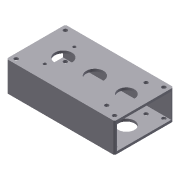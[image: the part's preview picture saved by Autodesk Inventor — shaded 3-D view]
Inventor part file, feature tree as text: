
AUTODESK INVENTOR PART (.ipt)
format: ipt  version: 2011 (Build 150239000, 239)  size: 154,112 bytes
history: native  units: in
note: dims shown in document units (in); Inventor stores cm internally (conversion verified against a paired STEP export)
features: other x1, imported_body x1, sketch x1
ambient origin geometry x8: Origin, YZ Plane, XZ Plane, XY Plane, X Axis, Y Axis, Z Axis, Center Point
feature tree (3):
  other  "Toughbox-nano-d01"
  imported_body  "Base1"
  sketch  "Sketch1"
